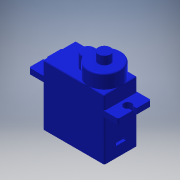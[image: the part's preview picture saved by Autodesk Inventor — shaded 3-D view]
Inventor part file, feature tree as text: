
AUTODESK INVENTOR PART (.ipt)
format: ipt  version: 2016 (Build 200138000, 138)  size: 240,128 bytes
history: native  units: in
note: dims shown in document units (in); Inventor stores cm internally (conversion verified against a paired STEP export)
features: sketch x6, other x4
ambient origin geometry x8: Origin, YZ Plane, XZ Plane, XY Plane, X Axis, Y Axis, Z Axis, Center Point
bodies: Solid1 (feature_tree)
feature tree (10):
  other  "Servo Motor SG90_correct_size.ipt"
  other  "솔리드1::Servo Motor SG90_correct_size.ipt"
  other  "TaggingFeature1"
  sketch  "스케치1"
  sketch  "스케치2"
  sketch  "스케치3"
  sketch  "스케치4"
  sketch  "스케치6"
  sketch  "Sketch7"  dims[d0=0.3937in]
  other  "작업 평면1"
